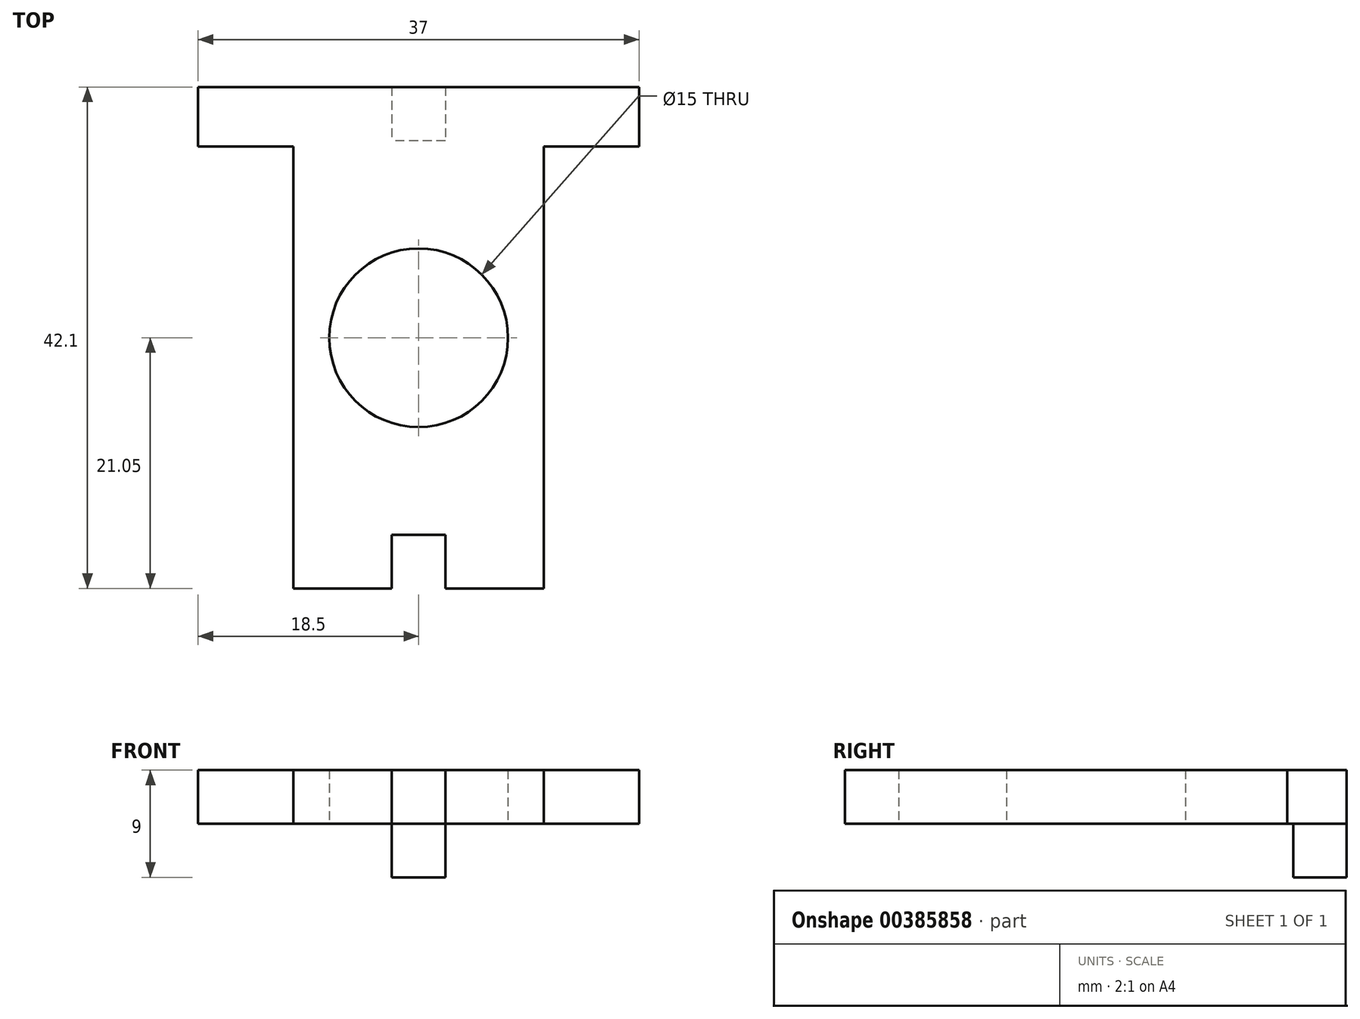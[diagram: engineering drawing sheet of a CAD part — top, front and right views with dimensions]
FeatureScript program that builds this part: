
annotation { "Feature Type Name" : "Feature", "Feature Type Description" : "" }
export const myFeature = defineFeature(function(context is Context, id is Id, definition is map)
    precondition{}
    {
        {
            var Q0;
            Q0=qCreatedBy(makeId("Top.planeOp"),FACE);
            var sketch = newSketch(context, id + "F0", { "sketchPlane" : qUnion([Q0])});
            skLineSegment(sketch, "E0.bottom", {"start": v(-10.5, 21.05) * mm, "end": v(10.5, 21.05) * mm});
            skLineSegment(sketch, "E0.top", {"start": v(-10.5, -21.05) * mm, "end": v(10.5, -21.05) * mm});
            skLineSegment(sketch, "E0.left", {"start": v(-10.5, 21.05) * mm, "end": v(-10.5, -21.05) * mm});
            skLineSegment(sketch, "E0.right", {"start": v(10.5, 21.05) * mm, "end": v(10.5, -21.05) * mm});
            skCircle(sketch, "E1", {"center": v(0, 0) * mm, "radius": 7.5 * mm});
            skLineSegment(sketch, "E2.bottom", {"start": v(2.25, -21.05) * mm, "end": v(-2.25, -21.05) * mm});
            skLineSegment(sketch, "E2.top", {"start": v(2.25, -16.55) * mm, "end": v(-2.25, -16.55) * mm});
            skLineSegment(sketch, "E2.left", {"start": v(2.25, -21.05) * mm, "end": v(2.25, -16.55) * mm});
            skLineSegment(sketch, "E2.right", {"start": v(-2.25, -21.05) * mm, "end": v(-2.25, -16.55) * mm});
            skSolve(sketch);
        }
        {
            var Q0;
            Q0=makeQuery(id+"F0.imprint","IMPRINT",FACE,{"disambiguationData":[TD([[makeQuery(id+"F0.imprint","IMPRINT",EDGE,{"derivedFrom":sQuery(id+"F0.wireOp",EDGE,"E0.bottom")}),-1.0]])]});
            extrude(context, id + "F1", {"entities" : qUnion([Q0]), "depth" : 4.5 * mm});
        }
        {
            var Q0;
            Q0=makeQuery(id+"F1.opExtrude","CAP_FACE",FACE,{"disambiguationData":[OSD([sQuery(id+"F0.wireOp",EDGE,"E0.bottom"),sQuery(id+"F0.wireOp",EDGE,"E0.top"),sQuery(id+"F0.wireOp",EDGE,"E0.left"),sQuery(id+"F0.wireOp",EDGE,"E0.right"),sQuery(id+"F0.wireOp",EDGE,"E1"),sQuery(id+"F0.wireOp",EDGE,"E2.top"),sQuery(id+"F0.wireOp",EDGE,"E2.left"),sQuery(id+"F0.wireOp",EDGE,"E2.right")])],"isStart":true});
            var sketch = newSketch(context, id + "F2", { "sketchPlane" : qUnion([Q0])});
            skLineSegment(sketch, "E3.bottom", {"start": v(2.25, -21.05) * mm, "end": v(-2.25, -21.05) * mm});
            skLineSegment(sketch, "E3.top", {"start": v(2.25, -16.55) * mm, "end": v(-2.25, -16.55) * mm});
            skLineSegment(sketch, "E3.left", {"start": v(2.25, -21.05) * mm, "end": v(2.25, -16.55) * mm});
            skLineSegment(sketch, "E3.right", {"start": v(-2.25, -21.05) * mm, "end": v(-2.25, -16.55) * mm});
            skSolve(sketch);
        }
        {
            var Q0;
            Q0 = qSketchRegion(id + "F2", true);
            extrude(context, id + "F3", {"entities" : qUnion([Q0]), "operationType" : NewBodyOperationType.ADD, "depth" : 4.5 * mm});
        }
        {
            var Q0;
            Q0=makeQuery(id+"F1.opExtrude","CAP_FACE",FACE,{"disambiguationData":[OSD([sQuery(id+"F0.wireOp",EDGE,"E0.bottom"),sQuery(id+"F0.wireOp",EDGE,"E0.top"),sQuery(id+"F0.wireOp",EDGE,"E0.left"),sQuery(id+"F0.wireOp",EDGE,"E0.right"),sQuery(id+"F0.wireOp",EDGE,"E1"),sQuery(id+"F0.wireOp",EDGE,"E2.top"),sQuery(id+"F0.wireOp",EDGE,"E2.left"),sQuery(id+"F0.wireOp",EDGE,"E2.right")])],"isStart":false});
            var sketch = newSketch(context, id + "F4", { "sketchPlane" : qUnion([Q0])});
            skLineSegment(sketch, "E4.bottom", {"start": v(-18.5, 21.05) * mm, "end": v(18.5, 21.05) * mm});
            skLineSegment(sketch, "E4.top", {"start": v(-18.5, 16.05) * mm, "end": v(18.5, 16.05) * mm});
            skLineSegment(sketch, "E4.left", {"start": v(-18.5, 21.05) * mm, "end": v(-18.5, 16.05) * mm});
            skLineSegment(sketch, "E4.right", {"start": v(18.5, 21.05) * mm, "end": v(18.5, 16.05) * mm});
            skSolve(sketch);
        }
        {
            var Q0;
            Q0 = qSketchRegion(id + "F4", true);
            extrude(context, id + "F5", {"entities" : qUnion([Q0]), "operationType" : NewBodyOperationType.ADD, "oppositeDirection" : true, "depth" : 4.5 * mm});
        }
    });
